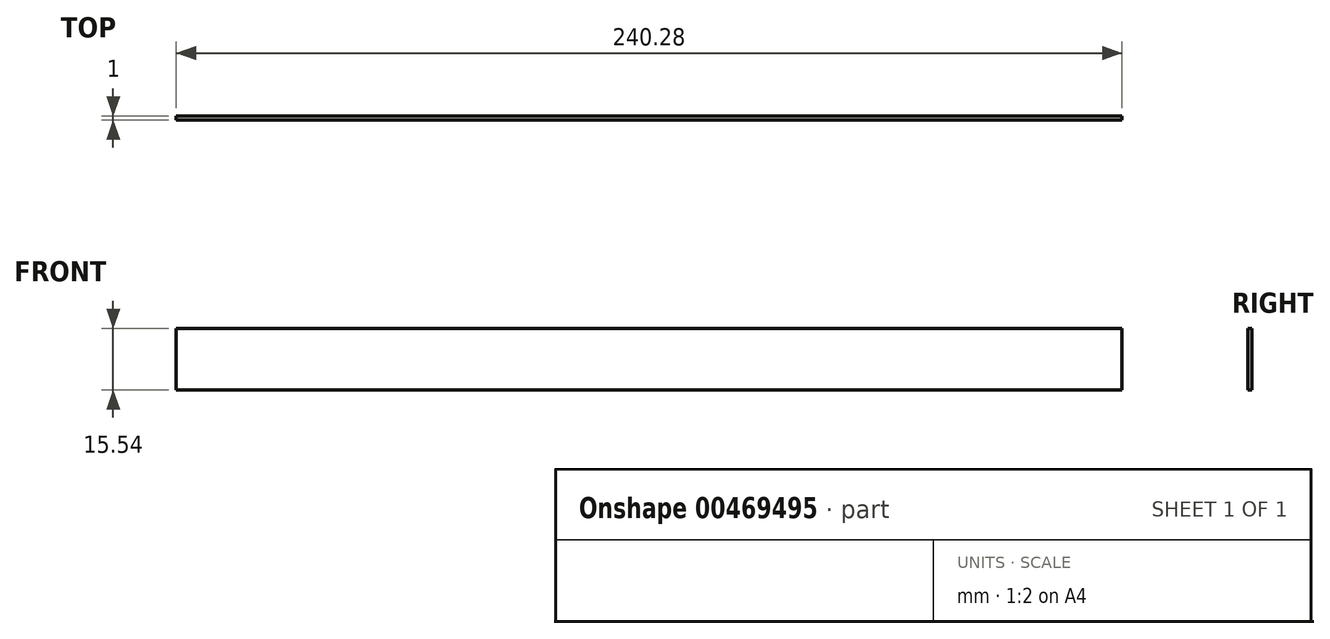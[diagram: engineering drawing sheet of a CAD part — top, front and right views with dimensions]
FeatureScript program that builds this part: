
annotation { "Feature Type Name" : "Feature", "Feature Type Description" : "" }
export const myFeature = defineFeature(function(context is Context, id is Id, definition is map)
    precondition{}
    {
        {
            var Q0;
            Q0=qCreatedBy(makeId("Front.planeOp"),FACE);
            var sketch = newSketch(context, id + "F0", { "sketchPlane" : qUnion([Q0])});
            skLineSegment(sketch, "E0.bottom", {"start": v(120.14, 7.77) * mm, "end": v(-120.14, 7.77) * mm});
            skLineSegment(sketch, "E0.top", {"start": v(120.14, -7.77) * mm, "end": v(-120.14, -7.77) * mm});
            skLineSegment(sketch, "E0.left", {"start": v(120.14, 7.77) * mm, "end": v(120.14, -7.77) * mm});
            skLineSegment(sketch, "E0.right", {"start": v(-120.14, 7.77) * mm, "end": v(-120.14, -7.77) * mm});
            skPoint(sketch, "E0.middle", {"position": v(0, 0) * mm});
            skSolve(sketch);
        }
        {
            var Q0;
            Q0=makeQuery(id+"F0.imprint","IMPRINT",FACE,{"disambiguationData":[TD([[makeQuery(id+"F0.imprint","IMPRINT",EDGE,{"derivedFrom":sQuery(id+"F0.wireOp",EDGE,"E0.bottom")}),1.0]])]});
            extrude(context, id + "F1", {"entities" : qUnion([Q0]), "depth" : 1 * mm});
        }
    });
